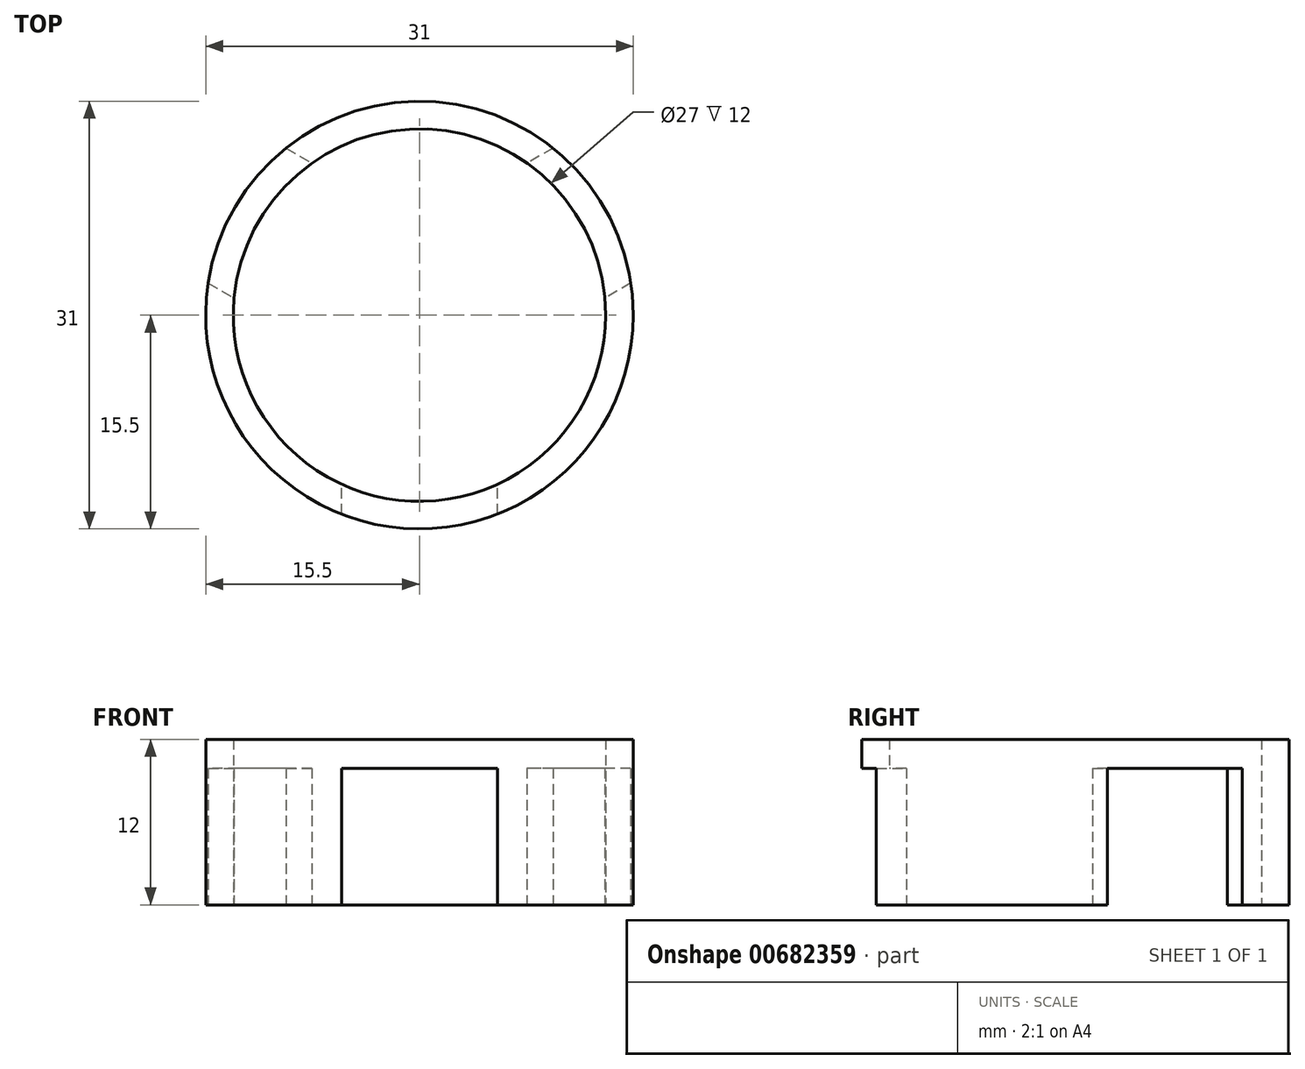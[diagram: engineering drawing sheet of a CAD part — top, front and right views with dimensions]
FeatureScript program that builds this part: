
annotation { "Feature Type Name" : "Feature", "Feature Type Description" : "" }
export const myFeature = defineFeature(function(context is Context, id is Id, definition is map)
    precondition{}
    {
        {
            var Q0;
            Q0=qCreatedBy(makeId("Top.planeOp"),FACE);
            var sketch = newSketch(context, id + "F0", { "sketchPlane" : qUnion([Q0])});
            skCircle(sketch, "E0", {"center": v(0, 0) * mm, "radius": 13.5 * mm});
            skCircle(sketch, "E1.0", {"center": v(0, 0) * mm, "radius": 15.5 * mm});
            skSolve(sketch);
        }
        {
            var Q0;
            Q0 = qSketchRegion(id + "F0", true);
            extrude(context, id + "F1", {"entities" : qUnion([Q0]), "depth" : 10 * mm, "offsetDistance" : 25 * mm});
        }
        {
            var Q0;
            Q0=qCreatedBy(makeId("Top.planeOp"),FACE);
            cPlane(context, id + "F2", {"entities" : qUnion([Q0]), "cplaneType" : CPlaneType.OFFSET, "offset" : 10 * mm, "width" : 150 * mm, "height" : 150 * mm});
        }
        {
            var Q0;
            Q0=qCreatedBy(id+"F2.planeOp",FACE);
            var sketch = newSketch(context, id + "F3", { "sketchPlane" : qUnion([Q0])});
            skCircle(sketch, "E2", {"center": v(0, 0) * mm, "radius": 15.5 * mm});
            skCircle(sketch, "E3.0", {"center": v(0, 0) * mm, "radius": 13.5 * mm});
            skSolve(sketch);
        }
        {
            var Q0;
            Q0 = qSketchRegion(id + "F3", true);
            extrude(context, id + "F4", {"entities" : qUnion([Q0]), "operationType" : NewBodyOperationType.ADD, "depth" : 2 * mm, "offsetDistance" : 25 * mm});
        }
        {
            var Q0;
            Q0=qCreatedBy(makeId("Top.planeOp"),FACE);
            var sketch = newSketch(context, id + "F5", { "sketchPlane" : qUnion([Q0])});
            skLineSegment(sketch, "E4.bottom", {"start": v(5.65, -22.17) * mm, "end": v(-5.65, -22.17) * mm});
            skLineSegment(sketch, "E4.top", {"start": v(5.65, -3.83) * mm, "end": v(-5.65, -3.83) * mm});
            skLineSegment(sketch, "E4.left", {"start": v(5.65, -22.17) * mm, "end": v(5.65, -3.83) * mm});
            skLineSegment(sketch, "E4.right", {"start": v(-5.65, -22.17) * mm, "end": v(-5.65, -3.83) * mm});
            skPoint(sketch, "E4.middle", {"position": v(0, 0) * mm});
            skSolve(sketch);
        }
        {
            var Q0;
            Q0 = qSketchRegion(id + "F5", true);
            extrude(context, id + "F6", {"entities" : qUnion([Q0]), "operationType" : NewBodyOperationType.REMOVE, "depth" : 9.9 * mm, "offsetDistance" : 25 * mm});
        }
        {
            var Q0;
            Q0=makeQuery(id+"F6.opExtrude","SWEPT_BODY",BODY,{"disambiguationData":[OSD([sQuery(id+"F5.wireOp",EDGE,"E4.bottom"),sQuery(id+"F5.wireOp",EDGE,"E4.top"),sQuery(id+"F5.wireOp",EDGE,"E4.left"),sQuery(id+"F5.wireOp",EDGE,"E4.right")])]});
            var Q1;
            Q1=makeQuery(id+"F6.boolean.opBoolean","COPY",FACE,{"derivedFrom":makeQuery(id+"F6.opExtrude","SWEPT_FACE",FACE,{"disambiguationData":[OSD([sQuery(id+"F5.wireOp",EDGE,"E4.right")])]})});
            var Q2;
            Q2=makeQuery(id+"F6.boolean.opBoolean","COPY",FACE,{"derivedFrom":makeQuery(id+"F6.opExtrude","CAP_FACE",FACE,{"disambiguationData":[OSD([sQuery(id+"F5.wireOp",EDGE,"E4.bottom"),sQuery(id+"F5.wireOp",EDGE,"E4.top"),sQuery(id+"F5.wireOp",EDGE,"E4.left"),sQuery(id+"F5.wireOp",EDGE,"E4.right")])],"isStart":false})});
            var Q3;
            Q3=makeQuery(id+"F6.boolean.opBoolean","COPY",FACE,{"derivedFrom":makeQuery(id+"F6.opExtrude","SWEPT_FACE",FACE,{"disambiguationData":[OSD([sQuery(id+"F5.wireOp",EDGE,"E4.left")])]})});
            var Q4;
            Q4=makeQuery(id+"F4.boolean.opBoolean","MERGE",FACE,{"derivedFrom":[makeQuery(id+"F1.opExtrude","SWEPT_FACE",FACE,{"disambiguationData":[OSD([sQuery(id+"F0.wireOp",EDGE,"E1.0")])]}),makeQuery(id+"F4.opExtrude","SWEPT_FACE",FACE,{"disambiguationData":[OSD([sQuery(id+"F3.wireOp",EDGE,"E2")])]})]});
            circularPattern(context, id + "F7", {"patternType" : PatternType.FACE, "faces" : qUnion([Q1, Q2, Q3]), "axis" : qUnion([Q4]), "angle" : 360 * degree, "instanceCount" : 3, "equalSpace" : true});
        }
        {
            var Q0;
            Q0=qCreatedBy(id+"F2.planeOp",FACE);
            cPlane(context, id + "F8", {"entities" : qUnion([Q0]), "cplaneType" : CPlaneType.OFFSET, "offset" : 12 * mm, "width" : 150 * mm, "height" : 150 * mm});
        }
        {
            var Q0;
            Q0=qCreatedBy(id+"F8.planeOp",FACE);
            var sketch = newSketch(context, id + "F9", { "sketchPlane" : qUnion([Q0])});
            skCircle(sketch, "E5", {"center": v(0, 0) * mm, "radius": 8 * mm});
            skCircle(sketch, "E6.0", {"center": v(0, 0) * mm, "radius": 10 * mm});
            skSolve(sketch);
        }
        {
            var Q0;
            Q0=makeQuery(id+"F9.imprint","IMPRINT",FACE,{"disambiguationData":[TD([[makeQuery(id+"F9.imprint","IMPRINT",EDGE,{"derivedFrom":sQuery(id+"F9.wireOp",EDGE,"E5")}),1.0]])]});
            extrude(context, id + "F10", {"entities" : qUnion([Q0]), "operationType" : NewBodyOperationType.REMOVE, "oppositeDirection" : true, "depth" : 25 * mm, "offsetDistance" : 25 * mm});
        }
        {
            var Q0;
            Q0=qCreatedBy(makeId("Front.planeOp"),FACE);
            var sketch = newSketch(context, id + "F11", { "sketchPlane" : qUnion([Q0])});
            skLineSegment(sketch, "E7", {"start": v(0, 0) * mm, "end": v(15.5, 0) * mm});
            skLineSegment(sketch, "E8", {"start": v(15.5, 0) * mm, "end": v(15.5, 12) * mm});
            skLineSegment(sketch, "E9", {"start": v(15.5, 12) * mm, "end": v(13.5, 12) * mm});
            skLineSegment(sketch, "E10", {"start": v(0, 0) * mm, "end": v(0, 17) * mm});
            skLineSegment(sketch, "E11", {"start": v(0, 17) * mm, "end": v(10, 17) * mm});
            skLineSegment(sketch, "E12", {"start": v(10, 17) * mm, "end": v(8, 17) * mm});
            skLineSegment(sketch, "E13", {"start": v(10, 17) * mm, "end": v(10, 22) * mm});
            skLineSegment(sketch, "E14.bottom", {"start": v(10, 22) * mm, "end": v(8, 22) * mm});
            skLineSegment(sketch, "E14.left", {"start": v(10, 22) * mm, "end": v(10, 17) * mm});
            skLineSegment(sketch, "E14.right", {"start": v(8, 22) * mm, "end": v(8, 17) * mm});
            skLineSegment(sketch, "E15", {"start": v(13.5, 12) * mm, "end": v(13.5, 11) * mm});
            skLineSegment(sketch, "E16.bottom", {"start": v(13.5, 11) * mm, "end": v(15.5, 11) * mm});
            skLineSegment(sketch, "E16.top", {"start": v(13.5, 12) * mm, "end": v(15.5, 12) * mm});
            skLineSegment(sketch, "E16.left", {"start": v(13.5, 11) * mm, "end": v(13.5, 12) * mm});
            skLineSegment(sketch, "E16.right", {"start": v(15.5, 11) * mm, "end": v(15.5, 12) * mm});
            skLineSegment(sketch, "E17", {"start": v(8, 17) * mm, "end": v(13.5, 12) * mm});
            skLineSegment(sketch, "E18", {"start": v(10, 17) * mm, "end": v(15.5, 12) * mm});
            skSolve(sketch);
        }
        {
            var Q0;
            Q0=sQuery(id+"F11.wireOp",EDGE,"E18");
            var Q1;
            Q1=sQuery(id+"F11.wireOp",EDGE,"E17");
            var Q2;
            Q2=sQuery(id+"F11.wireOp",EDGE,"E14.right");
            var Q3;
            Q3=sQuery(id+"F11.wireOp",EDGE,"E14.left");
            var Q4;
            Q4=sQuery(id+"F11.wireOp",EDGE,"E14.bottom");
            var Q5;
            Q5=sQuery(id+"F11.wireOp",EDGE,"E9");
            var Q6;
            Q6=sQuery(id+"F11.wireOp",EDGE,"E10");
            revolve(context, id + "F12", {"bodyType" : ToolBodyType.SURFACE, "surfaceEntities" : qUnion([Q0, Q1, Q2, Q3, Q4, Q5]), "axis" : qUnion([Q6]), "revolveType" : RevolveType.FULL});
        }
    });
